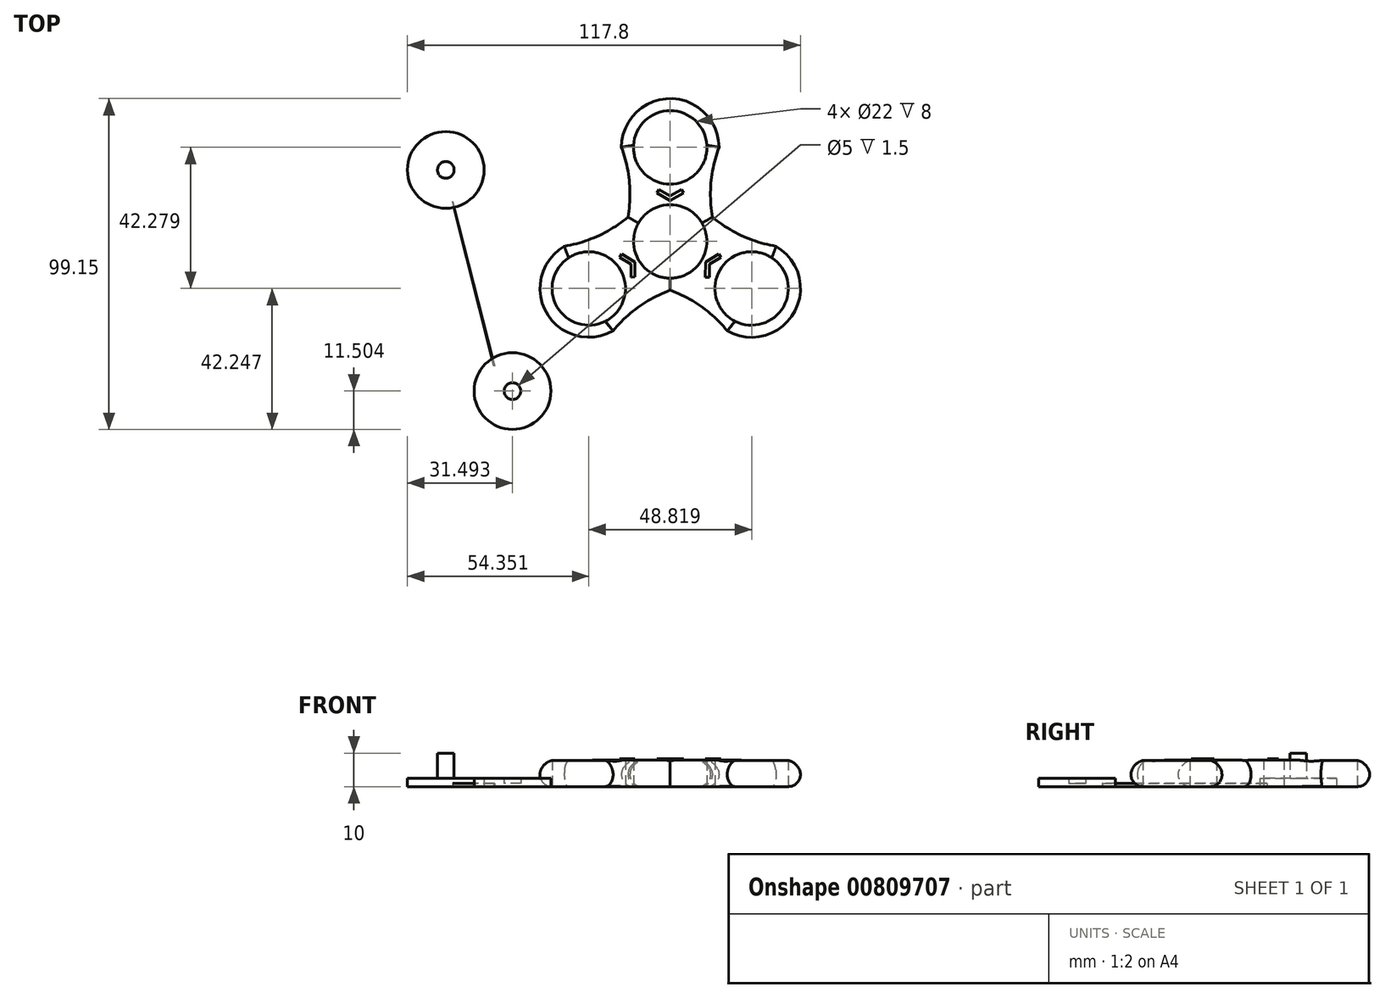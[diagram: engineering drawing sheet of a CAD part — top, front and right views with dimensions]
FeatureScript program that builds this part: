
annotation { "Feature Type Name" : "Feature", "Feature Type Description" : "" }
export const myFeature = defineFeature(function(context is Context, id is Id, definition is map)
    precondition{}
    {
        {
            var Q0;
            Q0=qCreatedBy(makeId("Top.planeOp"),FACE);
            var sketch = newSketch(context, id + "F0", { "sketchPlane" : qUnion([Q0])});
            skCircle(sketch, "E0", {"center": v(0, 0) * mm, "radius": 0.92 * mm});
            skCircle(sketch, "E1", {"center": v(0, 0) * mm, "radius": 11 * mm});
            skCircle(sketch, "E2", {"center": v(0, 28.19) * mm, "radius": 11 * mm});
            skArc(sketch, "E3", {"start": v(14.76, 28.19) * mm, "mid": v(0, 42.95) * mm, "end": v(-14.76, 28.19) * mm});
            skArc(sketch, "E4", {"start": v(14.76, 28.19) * mm, "mid": v(12.2, 14.1) * mm, "end": v(14.76, 0) * mm});
            skArc(sketch, "E5", {"start": v(-14.76, 0) * mm, "mid": v(-12.2, 14.1) * mm, "end": v(-14.76, 28.19) * mm});
            skArc(sketch, "E6.1.0", {"start": v(-31.8, -1.3) * mm, "mid": v(-18.3, 3.52) * mm, "end": v(-7.38, 12.78) * mm});
            skArc(sketch, "E6.1.1", {"start": v(-31.8, -1.3) * mm, "mid": v(-37.2, -21.47) * mm, "end": v(-17.03, -26.88) * mm});
            skArc(sketch, "E6.1.2", {"start": v(7.38, -12.78) * mm, "mid": v(-6.1, -17.6) * mm, "end": v(-17.03, -26.88) * mm});
            skCircle(sketch, "E6.1.3", {"center": v(-24.4, -14.1) * mm, "radius": 11 * mm});
            skArc(sketch, "E6.2.0", {"start": v(17.03, -26.88) * mm, "mid": v(6.1, -17.6) * mm, "end": v(-7.38, -12.78) * mm});
            skArc(sketch, "E6.2.1", {"start": v(17.03, -26.88) * mm, "mid": v(37.2, -21.47) * mm, "end": v(31.8, -1.3) * mm});
            skArc(sketch, "E6.2.2", {"start": v(7.38, 12.78) * mm, "mid": v(18.3, 3.52) * mm, "end": v(31.8, -1.3) * mm});
            skCircle(sketch, "E6.2.3", {"center": v(24.4, -14.1) * mm, "radius": 11 * mm});
            skSolve(sketch);
        }
        {
            var Q0;
            Q0=qSketchRegion(id+"F0",true);
            extrude(context, id + "F1", {"entities" : qUnion([Q0]), "depth" : 8 * mm, "offsetDistance" : 25 * mm});
        }
        {
            var Q0;
            Q0=qCreatedBy(makeId("Top.planeOp"),FACE);
            var sketch = newSketch(context, id + "F2", { "sketchPlane" : qUnion([Q0])});
            skCircle(sketch, "E7", {"center": v(-67.26, 21.43) * mm, "radius": 11.5 * mm});
            skCircle(sketch, "E8", {"center": v(-67.26, 21.43) * mm, "radius": 2.5 * mm});
            skSolve(sketch);
        }
        {
            var Q0;
            Q0=makeQuery(id+"F2.imprint","IMPRINT",FACE,{"disambiguationData":[TD([[makeQuery(id+"F2.imprint","IMPRINT",EDGE,{"derivedFrom":sQuery(id+"F2.wireOp",EDGE,"E7")}),1.0]])]});
            extrude(context, id + "F3", {"entities" : qUnion([Q0]), "depth" : 2.5 * mm, "offsetDistance" : 25 * mm});
        }
        {
            var Q0;
            Q0=makeQuery(id+"F2.imprint","IMPRINT",FACE,{"disambiguationData":[TD([[makeQuery(id+"F2.imprint","IMPRINT",EDGE,{"derivedFrom":sQuery(id+"F2.wireOp",EDGE,"E8")}),1.0]])]});
            extrude(context, id + "F4", {"entities" : qUnion([Q0]), "operationType" : NewBodyOperationType.ADD, "depth" : 10 * mm, "offsetDistance" : 25 * mm});
        }
        {
            var Q0;
            Q0=qCreatedBy(makeId("Top.planeOp"),FACE);
            var sketch = newSketch(context, id + "F5", { "sketchPlane" : qUnion([Q0])});
            skCircle(sketch, "E9", {"center": v(-47.27, -44.84) * mm, "radius": 11.5 * mm});
            skCircle(sketch, "E10", {"center": v(-47.27, -44.84) * mm, "radius": 2.5 * mm});
            skSolve(sketch);
        }
        {
            var Q0;
            Q0=qSketchRegion(id+"F5",true);
            extrude(context, id + "F6", {"entities" : qUnion([Q0]), "depth" : 2.5 * mm, "offsetDistance" : 25 * mm});
        }
        {
            var Q0;
            Q0=makeQuery(id+"F5.imprint","IMPRINT",FACE,{"disambiguationData":[TD([[makeQuery(id+"F5.imprint","IMPRINT",EDGE,{"derivedFrom":sQuery(id+"F5.wireOp",EDGE,"E10")}),1.0]])]});
            extrude(context, id + "F7", {"entities" : qUnion([Q0]), "operationType" : NewBodyOperationType.ADD, "depth" : 1 * mm, "offsetDistance" : 25 * mm});
        }
        {
            var Q0;
            Q0=qCreatedBy(makeId("Top.planeOp"),FACE);
            var sketch = newSketch(context, id + "F8", { "sketchPlane" : qUnion([Q0])});
            skLineSegment(sketch, "E11", {"start": v(-65.26, 12.04) * mm, "end": v(-52.63, -37.25) * mm});
            skLineSegment(sketch, "E12", {"start": v(-52.63, -37.25) * mm, "end": v(-52.85, -37.3) * mm});
            skLineSegment(sketch, "E13", {"start": v(-52.85, -37.3) * mm, "end": v(-65.26, 12.04) * mm});
            skSolve(sketch);
        }
        {
            var Q0;
            Q0=makeQuery(id+"F8.imprint","IMPRINT",FACE,{"disambiguationData":[TD([[makeQuery(id+"F8.imprint","IMPRINT",EDGE,{"derivedFrom":sQuery(id+"F8.wireOp",EDGE,"E11")}),-1.0]])]});
            extrude(context, id + "F9", {"entities" : qUnion([Q0]), "depth" : 0.9 * mm, "offsetDistance" : 25 * mm});
        }
        {
            var Q0;
            Q0=makeQuery(id+"F1.opExtrude","CAP_EDGE",EDGE,{"disambiguationData":[OSD([sQuery(id+"F0.wireOp",EDGE,"E6.1.2")])],"isStart":false});
            var Q1;
            Q1=makeQuery(id+"F1.opExtrude","CAP_EDGE",EDGE,{"disambiguationData":[OSD([sQuery(id+"F0.wireOp",EDGE,"E6.1.0")])],"isStart":false});
            var Q2;
            Q2=makeQuery(id+"F1.opExtrude","CAP_EDGE",EDGE,{"disambiguationData":[OSD([sQuery(id+"F0.wireOp",EDGE,"E5")])],"isStart":false});
            var Q3;
            Q3=makeQuery(id+"F1.opExtrude","CAP_EDGE",EDGE,{"disambiguationData":[OSD([sQuery(id+"F0.wireOp",EDGE,"E4")])],"isStart":false});
            var Q4;
            Q4=makeQuery(id+"F1.opExtrude","CAP_EDGE",EDGE,{"disambiguationData":[OSD([sQuery(id+"F0.wireOp",EDGE,"E6.2.2")])],"isStart":false});
            var Q5;
            Q5=makeQuery(id+"F1.opExtrude","CAP_EDGE",EDGE,{"disambiguationData":[OSD([sQuery(id+"F0.wireOp",EDGE,"E6.2.0")])],"isStart":false});
            var Q6;
            Q6=makeQuery(id+"F1.opExtrude","CAP_EDGE",EDGE,{"disambiguationData":[OSD([sQuery(id+"F0.wireOp",EDGE,"E6.2.1")])],"isStart":false});
            var Q7;
            Q7=makeQuery(id+"F1.opExtrude","CAP_EDGE",EDGE,{"disambiguationData":[OSD([sQuery(id+"F0.wireOp",EDGE,"E6.1.1")])],"isStart":false});
            var Q8;
            Q8=makeQuery(id+"F1.opExtrude","CAP_EDGE",EDGE,{"disambiguationData":[OSD([sQuery(id+"F0.wireOp",EDGE,"E3")])],"isStart":false});
            fillet(context, id + "F10", {"entities" : qUnion([Q0, Q1, Q2, Q3, Q4, Q5, Q6, Q7, Q8]), "radius" : 5 * mm, "tangentPropagation" : true, "allowEdgeOverflow" : false});
        }
        {
            var Q0;
            Q0=makeQuery(id+"F1.opExtrude","CAP_EDGE",EDGE,{"disambiguationData":[OSD([sQuery(id+"F0.wireOp",EDGE,"E6.1.2")])],"isStart":true});
            var Q1;
            Q1=makeQuery(id+"F1.opExtrude","CAP_EDGE",EDGE,{"disambiguationData":[OSD([sQuery(id+"F0.wireOp",EDGE,"E6.1.0")])],"isStart":true});
            var Q2;
            Q2=makeQuery(id+"F1.opExtrude","CAP_EDGE",EDGE,{"disambiguationData":[OSD([sQuery(id+"F0.wireOp",EDGE,"E6.2.0")])],"isStart":true});
            var Q3;
            Q3=makeQuery(id+"F1.opExtrude","CAP_EDGE",EDGE,{"disambiguationData":[OSD([sQuery(id+"F0.wireOp",EDGE,"E6.2.2")])],"isStart":true});
            var Q4;
            Q4=makeQuery(id+"F1.opExtrude","CAP_EDGE",EDGE,{"disambiguationData":[OSD([sQuery(id+"F0.wireOp",EDGE,"E5")])],"isStart":true});
            var Q5;
            Q5=makeQuery(id+"F1.opExtrude","CAP_EDGE",EDGE,{"disambiguationData":[OSD([sQuery(id+"F0.wireOp",EDGE,"E4")])],"isStart":true});
            var Q6;
            Q6=makeQuery(id+"F1.opExtrude","CAP_EDGE",EDGE,{"disambiguationData":[OSD([sQuery(id+"F0.wireOp",EDGE,"E3")])],"isStart":true});
            var Q7;
            Q7=makeQuery(id+"F1.opExtrude","CAP_EDGE",EDGE,{"disambiguationData":[OSD([sQuery(id+"F0.wireOp",EDGE,"E6.1.1")])],"isStart":true});
            var Q8;
            Q8=makeQuery(id+"F1.opExtrude","CAP_EDGE",EDGE,{"disambiguationData":[OSD([sQuery(id+"F0.wireOp",EDGE,"E6.2.1")])],"isStart":true});
            fillet(context, id + "F11", {"entities" : qUnion([Q0, Q1, Q2, Q3, Q4, Q5, Q6, Q7, Q8]), "radius" : 3.6 * mm, "tangentPropagation" : true, "allowEdgeOverflow" : false});
        }
        {
            var Q0;
            Q0=qCreatedBy(makeId("Top.planeOp"),FACE);
            var sketch = newSketch(context, id + "F12", { "sketchPlane" : qUnion([Q0])});
            skLineSegment(sketch, "E14", {"start": v(0, 12.25) * mm, "end": v(-3.96, 14.49) * mm});
            skLineSegment(sketch, "E15", {"start": v(-3.96, 14.49) * mm, "end": v(-3.38, 15.52) * mm});
            skLineSegment(sketch, "E16", {"start": v(-3.38, 15.52) * mm, "end": v(0, 13.61) * mm});
            skLineSegment(sketch, "E17", {"start": v(0, 13.61) * mm, "end": v(3.4, 15.52) * mm});
            skLineSegment(sketch, "E18", {"start": v(3.4, 15.52) * mm, "end": v(3.98, 14.49) * mm});
            skLineSegment(sketch, "E19", {"start": v(3.98, 14.49) * mm, "end": v(0, 12.25) * mm});
            skLineSegment(sketch, "E20.1.0", {"start": v(-14.54, -3.8) * mm, "end": v(-10.6, -6.13) * mm});
            skLineSegment(sketch, "E20.1.1", {"start": v(-11.8, -6.8) * mm, "end": v(-15.14, -4.82) * mm});
            skLineSegment(sketch, "E20.1.2", {"start": v(-10.6, -6.13) * mm, "end": v(-10.56, -10.68) * mm});
            skLineSegment(sketch, "E20.1.3", {"start": v(-11.75, -10.69) * mm, "end": v(-11.8, -6.8) * mm});
            skLineSegment(sketch, "E20.1.4", {"start": v(-10.56, -10.68) * mm, "end": v(-11.75, -10.69) * mm});
            skLineSegment(sketch, "E20.1.5", {"start": v(-15.14, -4.82) * mm, "end": v(-14.54, -3.8) * mm});
            skLineSegment(sketch, "E20.2.0", {"start": v(10.56, -10.69) * mm, "end": v(10.6, -6.13) * mm});
            skLineSegment(sketch, "E20.2.1", {"start": v(11.8, -6.8) * mm, "end": v(11.74, -10.7) * mm});
            skLineSegment(sketch, "E20.2.2", {"start": v(10.6, -6.13) * mm, "end": v(14.53, -3.81) * mm});
            skLineSegment(sketch, "E20.2.3", {"start": v(15.13, -4.83) * mm, "end": v(11.8, -6.8) * mm});
            skLineSegment(sketch, "E20.2.4", {"start": v(14.53, -3.81) * mm, "end": v(15.13, -4.83) * mm});
            skLineSegment(sketch, "E20.2.5", {"start": v(11.74, -10.7) * mm, "end": v(10.56, -10.69) * mm});
            skPoint(sketch, "E20.center", {"position": v(0, 0) * mm});
            skSolve(sketch);
        }
        {
            var Q0;
            Q0 = qSketchRegion(id + "F12", true);
            extrude(context, id + "F13", {"entities" : qUnion([Q0]), "operationType" : NewBodyOperationType.ADD, "depth" : 8.3 * mm, "offsetDistance" : 25 * mm});
        }
    });
